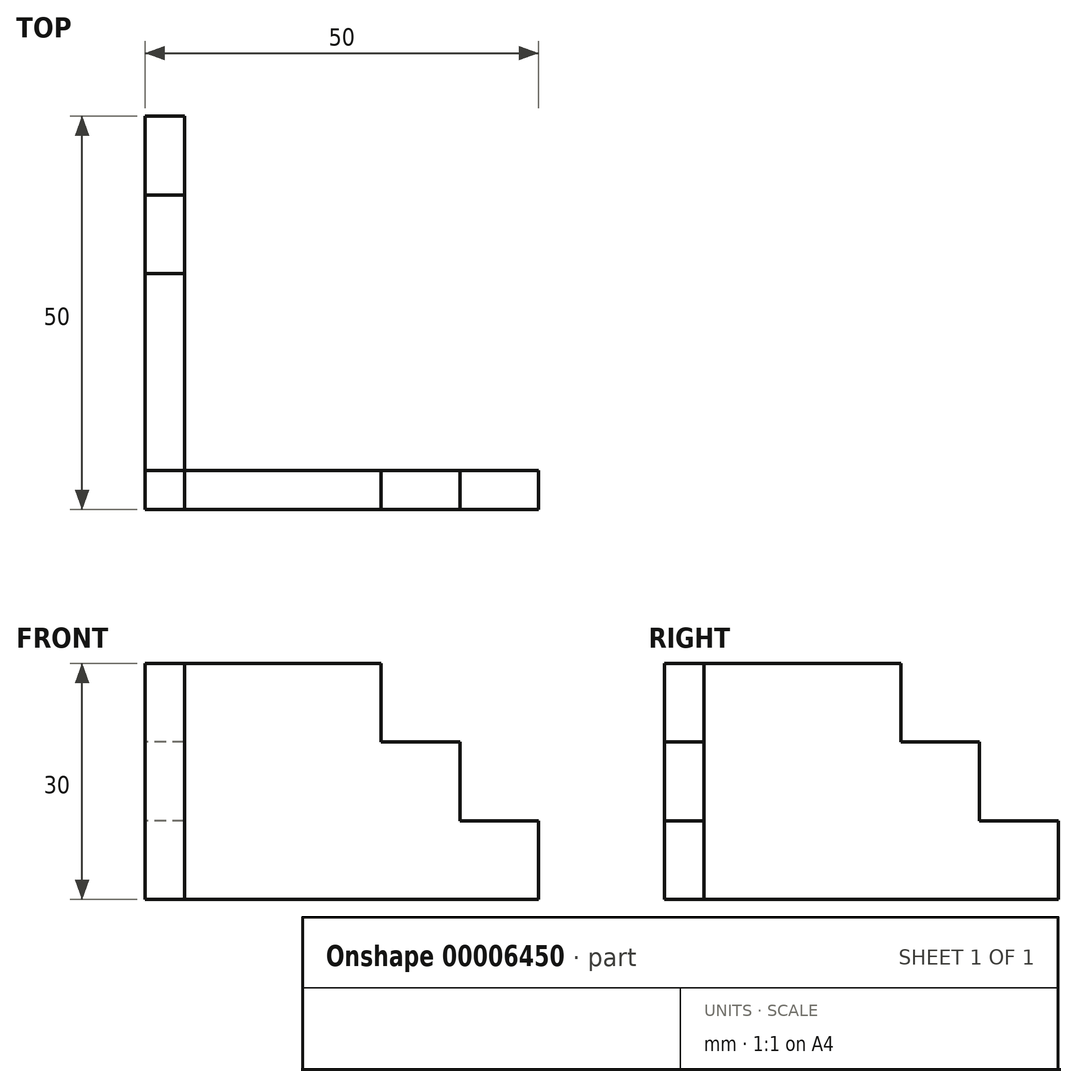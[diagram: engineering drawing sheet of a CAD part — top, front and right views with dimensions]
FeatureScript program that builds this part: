
annotation { "Feature Type Name" : "Feature", "Feature Type Description" : "" }
export const myFeature = defineFeature(function(context is Context, id is Id, definition is map)
    precondition{}
    {
        {
            var Q0;
            Q0=qCreatedBy(makeId("Front.planeOp"),FACE);
            var sketch = newSketch(context, id + "F0", { "sketchPlane" : qUnion([Q0])});
            skLineSegment(sketch, "E0", {"start": v(0, 0) * mm, "end": v(50, 0) * mm});
            skLineSegment(sketch, "E1", {"start": v(50, 0) * mm, "end": v(50, 10) * mm});
            skLineSegment(sketch, "E2", {"start": v(50, 10) * mm, "end": v(40, 10) * mm});
            skLineSegment(sketch, "E3", {"start": v(40, 10) * mm, "end": v(40, 20) * mm});
            skLineSegment(sketch, "E4", {"start": v(40, 20) * mm, "end": v(30, 20) * mm});
            skLineSegment(sketch, "E5", {"start": v(30, 20) * mm, "end": v(30, 30) * mm});
            skLineSegment(sketch, "E6", {"start": v(30, 30) * mm, "end": v(0, 30) * mm});
            skLineSegment(sketch, "E7", {"start": v(0, 30) * mm, "end": v(0, 0) * mm});
            skSolve(sketch);
        }
        {
            var Q0;
            Q0=makeQuery(id+"F0.imprint","IMPRINT",FACE,{"disambiguationData":[TD([[makeQuery(id+"F0.imprint","IMPRINT",EDGE,{"derivedFrom":sQuery(id+"F0.wireOp",EDGE,"E0")}),1.0]])]});
            extrude(context, id + "F1", {"entities" : qUnion([Q0]), "depth" : 5 * mm});
        }
        {
            var Q0;
            Q0=makeQuery(id+"F1.opExtrude","SWEPT_FACE",FACE,{"disambiguationData":[OSD([sQuery(id+"F0.wireOp",EDGE,"E7")])]});
            cPlane(context, id + "F2", {"entities" : qUnion([Q0]), "cplaneType" : CPlaneType.OFFSET, "offset" : 2.5 * mm, "oppositeDirection" : true, "width" : 150 * mm, "height" : 150 * mm});
        }
        {
            var Q0;
            Q0=makeQuery(id+"F1.opExtrude","CAP_FACE",FACE,{"disambiguationData":[OSD([sQuery(id+"F0.wireOp",EDGE,"E0"),sQuery(id+"F0.wireOp",EDGE,"E1"),sQuery(id+"F0.wireOp",EDGE,"E2"),sQuery(id+"F0.wireOp",EDGE,"E3"),sQuery(id+"F0.wireOp",EDGE,"E4"),sQuery(id+"F0.wireOp",EDGE,"E5"),sQuery(id+"F0.wireOp",EDGE,"E6"),sQuery(id+"F0.wireOp",EDGE,"E7")])],"isStart":false});
            cPlane(context, id + "F3", {"entities" : qUnion([Q0]), "cplaneType" : CPlaneType.OFFSET, "offset" : 2.5 * mm, "oppositeDirection" : true, "width" : 150 * mm, "height" : 150 * mm});
        }
        {
            var Q0;
            Q0=qCreatedBy(id+"F3.planeOp",FACE);
            var sketch = newSketch(context, id + "F4", { "sketchPlane" : qUnion([Q0])});
            skLineSegment(sketch, "E8", {"start": v(2.5, 75.78) * mm, "end": v(2.5, 43.34) * mm});
            skSolve(sketch);
        }
        {
            var Q0;
            Q0=makeQuery(id+"F1.opExtrude","SWEPT_BODY",BODY,{"disambiguationData":[OSD([sQuery(id+"F0.wireOp",EDGE,"E0"),sQuery(id+"F0.wireOp",EDGE,"E1"),sQuery(id+"F0.wireOp",EDGE,"E2"),sQuery(id+"F0.wireOp",EDGE,"E3"),sQuery(id+"F0.wireOp",EDGE,"E4"),sQuery(id+"F0.wireOp",EDGE,"E5"),sQuery(id+"F0.wireOp",EDGE,"E6"),sQuery(id+"F0.wireOp",EDGE,"E7")])]});
            var Q1;
            Q1=sQuery(id+"F4.wireOp",EDGE,"E8");
            circularPattern(context, id + "F5", {"entities" : qUnion([Q0]), "axis" : qUnion([Q1]), "angle" : 270 * degree, "instanceCount" : 2});
        }
    });
